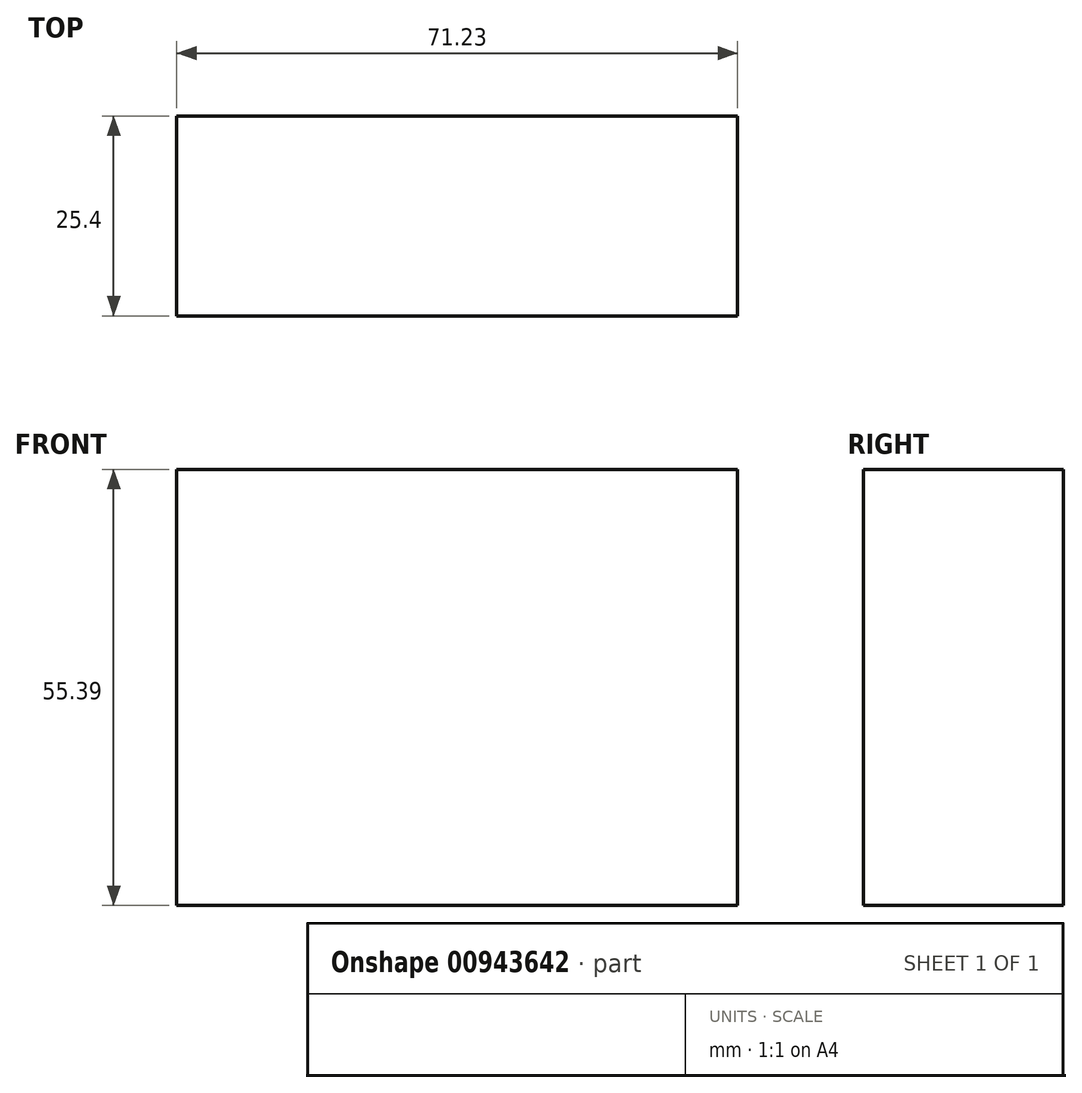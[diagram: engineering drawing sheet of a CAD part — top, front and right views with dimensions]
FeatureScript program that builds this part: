
annotation { "Feature Type Name" : "Feature", "Feature Type Description" : "" }
export const myFeature = defineFeature(function(context is Context, id is Id, definition is map)
    precondition{}
    {
        {
            var Q0;
            Q0=qCreatedBy(makeId("Front.planeOp"),FACE);
            var sketch = newSketch(context, id + "F0", { "sketchPlane" : qUnion([Q0])});
            skLineSegment(sketch, "E0.bottom", {"start": v(-51.28, 40.55) * mm, "end": v(19.95, 40.55) * mm});
            skLineSegment(sketch, "E0.top", {"start": v(-51.28, -14.84) * mm, "end": v(19.95, -14.84) * mm});
            skLineSegment(sketch, "E0.left", {"start": v(-51.28, 40.55) * mm, "end": v(-51.28, -14.84) * mm});
            skLineSegment(sketch, "E0.right", {"start": v(19.95, 40.55) * mm, "end": v(19.95, -14.84) * mm});
            skSolve(sketch);
        }
        {
            var Q0;
            Q0=makeQuery(id+"F0.imprint","IMPRINT",FACE,{"disambiguationData":[TD([[makeQuery(id+"F0.imprint","IMPRINT",EDGE,{"derivedFrom":sQuery(id+"F0.wireOp",EDGE,"E0.bottom")}),-1.0]])]});
            extrude(context, id + "F1", {"entities" : qUnion([Q0]), "depth" : 25.4 * mm, "offsetDistance" : 25.4 * mm});
        }
    });
